# Revit family: Sideboard-Teknion-CFATE_Figure_29H_Triple_Sideboard_Elevated_Base-R2023
name_source: partatom
category: Furniture
units: mm (PartAtom-declared; Revit-internal decimal feet)

## family parameters
Always vertical = Yes
Cut with Voids When Loaded = No
Enable Cutting in Views = No
OmniClass Number = 23.40.20.00
OmniClass Title = General Furniture and Specialties
Render Appearance Source = Family Geometry
Room Calculation Point = No
Shared = Yes
Work Plane-Based = No

## types (6) — shared parameters
Assembly Code = E2020200
Glide Finish = Paint-Teknion-23-Z-Foundation-Foundry Onyx
Manufacturer = Teknion
Manufacturer Fax = 416.661.4586
Part Number = CFATE
Product Documentation Link = https://d2r72yk5wmppdj.cloudfront.net
Product Line = Figure - Sideboards
Product Page URL = https://www.teknion.com
Series = Custom Wood
Sustainability Data = https://www.teknion.com
URL = www.teknion.com
Unit Weight URL = http://www.teknion.com
Warranty = http://www.teknion.com
zero-valued in all types: Default Elevation

## per-type parameters (varying)
| type | Description | HCH | HDH | HHH | HWH | Model | WCW | WDW |
| All H.Doors | Figure - 29H Triple Sideboard, Elevated Base, All H.Doors | No | No | Yes | No | CFATE_HHH_______ | No | No |
| H.Door / Cutouts for AV or Fridge / H.Door | Figure - 29H Triple Sideboard, Elevated Base, H.Door / Cutouts for AV or Fridge / H.Door | Yes | No | No | No | CFATE_HCH_______ | No | No |
| Waste / Cutouts for AV or Fridge / Waste | Figure - 29H Triple Sideboard, Elevated Base, Waste / Cutouts for AV or Fridge / Waste | No | No | No | No | CFATE_WCW_______ | Yes | No |
| Waste / Casual Drawer / Waste | Figure - 29H Triple Sideboard, Elevated Base, Waste / Casual Drawer / Waste | No | No | No | No | CFATE_HWH_______ | No | Yes |
| H.Door / Waste / H.Door | Figure - 29H Triple Sideboard, Elevated Base, H.Door / Waste / H.Door | No | No | No | Yes | CFATE_HWH_______ | No | No |
| H.Door / Casual Drawer / H.Door | Figure - 29H Triple Sideboard, Elevated Base, H.Door / Casual Drawer / H.Door | No | Yes | No | No | CFATE_HDH_______ | No | No |

## geometry (parser evidence)
native form markers: Sweep x7
no freeform markers — native parametric forms only
